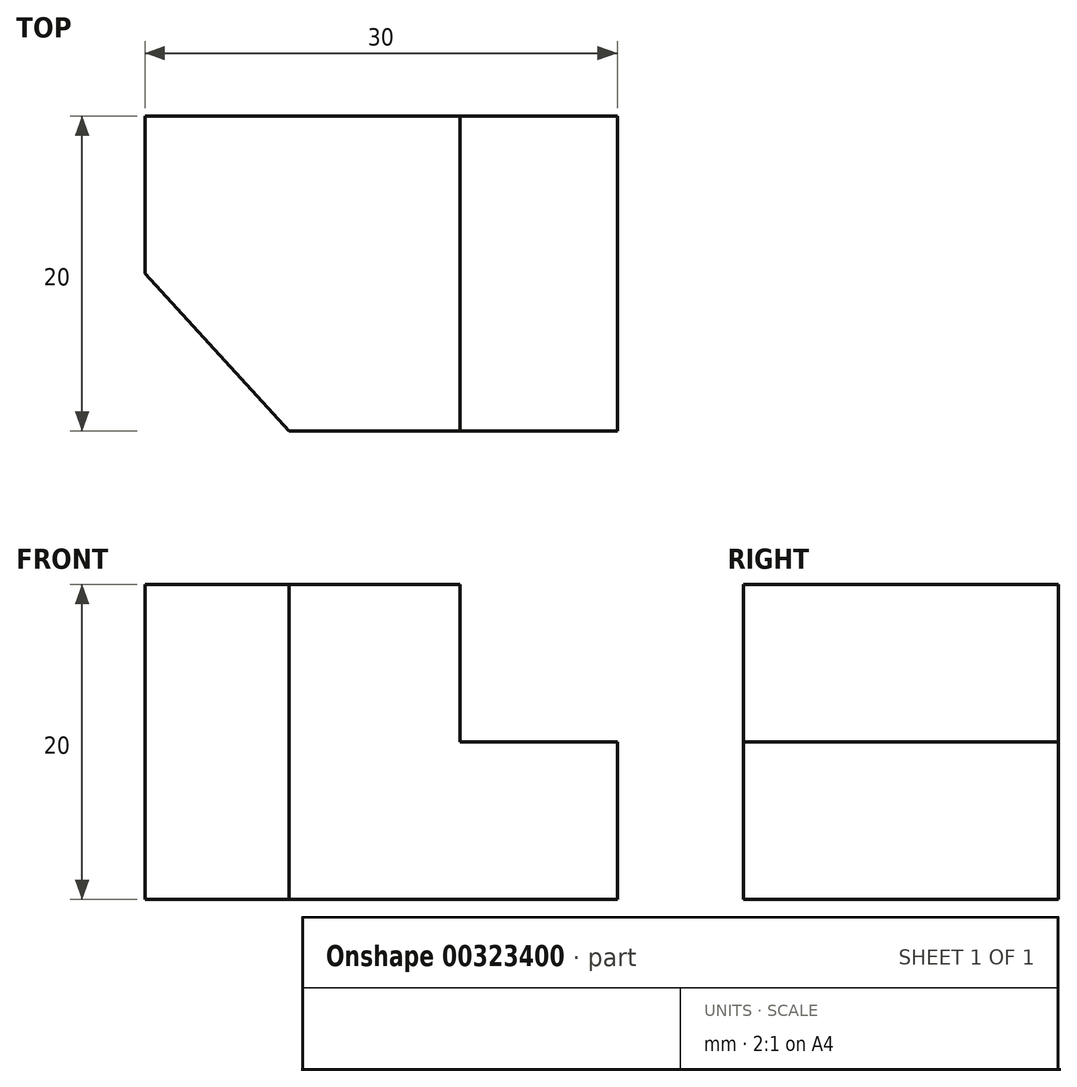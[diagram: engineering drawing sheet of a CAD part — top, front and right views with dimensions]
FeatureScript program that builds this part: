
annotation { "Feature Type Name" : "Feature", "Feature Type Description" : "" }
export const myFeature = defineFeature(function(context is Context, id is Id, definition is map)
    precondition{}
    {
        {
            var Q0;
            Q0=qCreatedBy(makeId("Top.planeOp"),FACE);
            var sketch = newSketch(context, id + "F0", { "sketchPlane" : qUnion([Q0])});
            skLineSegment(sketch, "E0", {"start": v(0, 0) * mm, "end": v(0, 10) * mm});
            skLineSegment(sketch, "E1", {"start": v(0, 10) * mm, "end": v(20, 10) * mm});
            skLineSegment(sketch, "E2", {"start": v(20, 10) * mm, "end": v(20, -10) * mm});
            skLineSegment(sketch, "E3", {"start": v(20, -10) * mm, "end": v(9.14, -10) * mm});
            skLineSegment(sketch, "E4", {"start": v(9.14, -10) * mm, "end": v(0, 0) * mm});
            skSolve(sketch);
        }
        {
            var Q0;
            Q0 = qSketchRegion(id + "F0", true);
            extrude(context, id + "F1", {"entities" : qUnion([Q0]), "depth" : 20 * mm});
        }
        {
            var Q0;
            Q0=makeQuery(id+"F1.opExtrude","SWEPT_FACE",FACE,{"disambiguationData":[OSD([sQuery(id+"F0.wireOp",EDGE,"E2")])]});
            var sketch = newSketch(context, id + "F2", { "sketchPlane" : qUnion([Q0])});
            skLineSegment(sketch, "E5.bottom", {"start": v(10, 0) * mm, "end": v(10, 0) * mm});
            skLineSegment(sketch, "E5.top", {"start": v(10, 10) * mm, "end": v(10, 10) * mm});
            skLineSegment(sketch, "E5.left", {"start": v(10, 0) * mm, "end": v(10, 10) * mm});
            skLineSegment(sketch, "E5.right", {"start": v(10, 0) * mm, "end": v(10, 10) * mm});
            skLineSegment(sketch, "E6", {"start": v(10, 10) * mm, "end": v(-10, 10) * mm});
            skLineSegment(sketch, "E7", {"start": v(-10, 10) * mm, "end": v(-10, 0) * mm});
            skLineSegment(sketch, "E8", {"start": v(-10, 0) * mm, "end": v(10, 0) * mm});
            skSolve(sketch);
        }
        {
            var Q0;
            Q0 = qSketchRegion(id + "F2", true);
            extrude(context, id + "F3", {"entities" : qUnion([Q0]), "operationType" : NewBodyOperationType.ADD, "depth" : 10 * mm});
        }
    });
